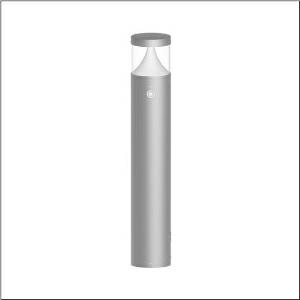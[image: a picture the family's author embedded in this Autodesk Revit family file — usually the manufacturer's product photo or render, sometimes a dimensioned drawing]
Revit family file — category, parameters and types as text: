
# Revit family: cl_31_poller_90_sensor_5cl444803
name_source: partatom
category: Lighting Fixtures
units: mm (PartAtom-declared; Revit-internal decimal feet)

## family parameters
Cut with Voids When Loaded = No
Host = Face
Light Source = No
Part Type = Normal
Room Calculation Point = No
Round Connector Dimension = Use Diameter
Shared = No

## types (1)
- --- (1 x LED, 1500 lm, 14 W, 3000K)
    Apparent Load = 14 VA
    CIE Flux Codes = 19 66 88 92 100
    Color Rendering = 80
    Color Temperature = 3000K
    Default Elevation = 1800 mm
    Description = CL 31 Bollard 90 Sensor, bollard luminaire, primary light control with lens, of PC, primary optical cover: cover panel, of PC, transparent, secondary light control with reflector, of PC, primary light characteristic: asymmetric, LED, rated luminous flux: 1.500lm, luminous efficacy: 107lm/W, light colour: 830, colour temperature: 3000K, control gear: ECG DALI, with terminal, 5-pole, max. 2.5mm², mains connection: 220..240V, AC, 50/60Hz, rated input power: 14W, luminaire housing, of aluminium, powder-coated, Siteco® metallic grey, diameter: 170mm, height: 900mm, PIR sensor, protection rating (complete): IP65, insulation class (complete): insulation class I (protective earthing), certification: CE, ENEC, impact resistance: IK08, permissible operating ambient temperature for outdoor applications: -20..+50°C, packaging unit: 1 piece
    Height = 200 mm  [stored 0.656168 ft]
    Lamp = 1 x LED
    Lamp Light Flux = 1500 lm
    Lamp Power = 14 W
    Lamp count = 1
    Length = 170 mm  [stored 0.557743 ft]
    Luminous efficacy = 107 lm/W
    Manufacturer = Siteco
    ModVariant = No
    Model = 5CL444803
    Mounting Place = Floor
    Mounting Type = Freestanding
    Number of Poles = 1
    OnlyDefault = Yes
    Power Factor = 1
    Product Name = CL 31 Poller 90 Sensor
    Product group = bollard luminaire | freestanding
    ProductGroupID = 1303
    Protection Class = Protection class I
    Protection Degree = IP 65
    RLX_Detail_Level = 1
    RlxData = <blob elided: 66345 chars, md5=e3eaab2b>
    Socket = socket
    Standby Power = 0 W
    System Light Flux = 1500 lm
    System Power = 14 W
    Type Comments = factory setting: luminous flux: 100 % | dim-lin: 254 | 350 mA
    Type Image = l_1006897.jpg
    URL = http://relux.com
    VarID = @adj_116859
    Voltage = 0 V
    Weight = 0.00 kg
    Width = 0 mm  [stored 0 ft]

note: [stored X ft] marks values corroborated as IEEE doubles in the binary element streams (Revit-internal decimal feet)

## geometry (parser evidence)
native form markers: Blend x4, Sweep x11
no freeform markers — native parametric forms only
